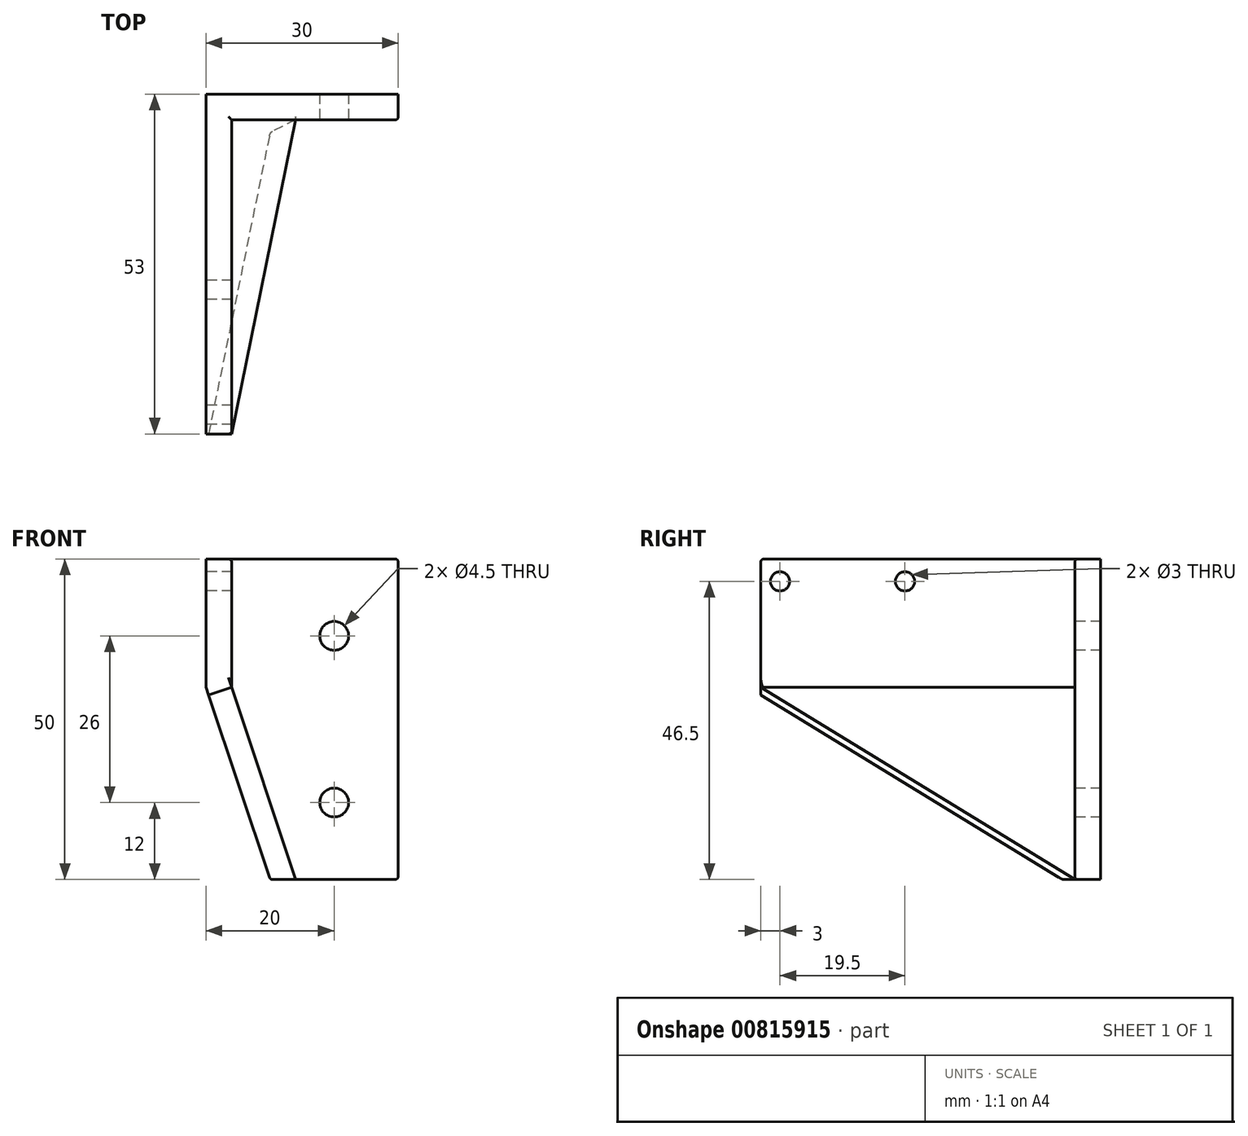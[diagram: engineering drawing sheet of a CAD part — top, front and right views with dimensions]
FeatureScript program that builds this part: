
annotation { "Feature Type Name" : "Feature", "Feature Type Description" : "" }
export const myFeature = defineFeature(function(context is Context, id is Id, definition is map)
    precondition{}
    {
        {
            var Q0;
            Q0=qCreatedBy(makeId("Front.planeOp"),FACE);
            var sketch = newSketch(context, id + "F0", { "sketchPlane" : qUnion([Q0])});
            skLineSegment(sketch, "E0.bottom", {"start": v(-15, 25) * mm, "end": v(15, 25) * mm});
            skLineSegment(sketch, "E0.top", {"start": v(-15, -25) * mm, "end": v(15, -25) * mm});
            skLineSegment(sketch, "E0.left", {"start": v(-15, 25) * mm, "end": v(-15, -25) * mm});
            skLineSegment(sketch, "E0.right", {"start": v(15, 25) * mm, "end": v(15, -25) * mm});
            skPoint(sketch, "E0.middle", {"position": v(0, 0) * mm});
            skLineSegment(sketch, "E1.bottom", {"start": v(-15, 25) * mm, "end": v(-11, 25) * mm});
            skLineSegment(sketch, "E1.top", {"start": v(-15, 5) * mm, "end": v(-11, 5) * mm});
            skLineSegment(sketch, "E1.left", {"start": v(-15, 25) * mm, "end": v(-15, 5) * mm});
            skLineSegment(sketch, "E1.right", {"start": v(-11, 25) * mm, "end": v(-11, 5) * mm});
            skCircle(sketch, "E2", {"center": v(5, 13) * mm, "radius": 2.25 * mm});
            skCircle(sketch, "E3", {"center": v(5, -13) * mm, "radius": 2.25 * mm});
            skPoint(sketch, "E4", {"position": v(-5, -25) * mm});
            skLineSegment(sketch, "E5", {"start": v(-15, 5) * mm, "end": v(-5, -25) * mm});
            skLineSegment(sketch, "E6", {"start": v(-11, 5) * mm, "end": v(-1, -25) * mm});
            skSolve(sketch);
        }
        {
            var Q0;
            {var subQ1=sQuery(id+"F0.wireOp",EDGE,"E0.right");Q0=makeQuery(id+"F0.imprint","IMPRINT",FACE,{"disambiguationData":[TD([[makeQuery(id+"F0.imprint","IMPRINT",EDGE,{"derivedFrom":subQ1}),-1.0]])]});}
            var Q1;
            {var subQ4=sQuery(id+"F0.wireOp",EDGE,"E1.top");Q1=makeQuery(id+"F0.imprint","IMPRINT",FACE,{"disambiguationData":[TD([[makeQuery(id+"F0.imprint","IMPRINT",EDGE,{"derivedFrom":subQ4}),1.0]])]});}
            var Q2;
            Q2=makeQuery(id+"F0.imprint","IMPRINT",FACE,{"disambiguationData":[TD([[makeQuery(id+"F0.imprint","IMPRINT",EDGE,{"derivedFrom":sQuery(id+"F0.wireOp",EDGE,"E1.top")}),-1.0]])]});
            extrude(context, id + "F1", {"entities" : qUnion([Q0, Q1, Q2]), "oppositeDirection" : true, "depth" : 4 * mm, "offsetDistance" : 25 * mm});
        }
        {
            var Q0;
            Q0=makeQuery(id+"F1.opExtrude","CAP_FACE",FACE,{"disambiguationData":[OSD([sQuery(id+"F0.wireOp",EDGE,"E0.bottom"),sQuery(id+"F0.wireOp",EDGE,"E0.top"),sQuery(id+"F0.wireOp",EDGE,"E0.left"),sQuery(id+"F0.wireOp",EDGE,"E0.right"),sQuery(id+"F0.wireOp",EDGE,"E2"),sQuery(id+"F0.wireOp",EDGE,"E3"),sQuery(id+"F0.wireOp",EDGE,"E5")])],"isStart":true});
            var sketch = newSketch(context, id + "F2", { "sketchPlane" : qUnion([Q0])});
            skLineSegment(sketch, "E7.bottom", {"start": v(-15, 25) * mm, "end": v(-11, 25) * mm});
            skLineSegment(sketch, "E7.top", {"start": v(-15, 5) * mm, "end": v(-11, 5) * mm});
            skLineSegment(sketch, "E7.left", {"start": v(-15, 25) * mm, "end": v(-15, 5) * mm});
            skLineSegment(sketch, "E7.right", {"start": v(-11, 25) * mm, "end": v(-11, 5) * mm});
            skLineSegment(sketch, "E8", {"start": v(-11, 5) * mm, "end": v(-1, -25) * mm});
            skSolve(sketch);
        }
        {
            var Q0;
            Q0 = qSketchRegion(id + "F2", true);
            var Q1;
            Q1=makeQuery(id+"F2.imprint","IMPRINT",FACE,{"disambiguationData":[TD([[makeQuery(id+"F2.imprint","IMPRINT",EDGE,{"derivedFrom":sQuery(id+"F2.wireOp",EDGE,"E7.top")}),-1.0]])]});
            extrude(context, id + "F3", {"entities" : qUnion([Q0, Q1]), "operationType" : NewBodyOperationType.ADD, "depth" : 49 * mm, "offsetDistance" : 25 * mm});
        }
        {
            var Q0;
            Q0=makeQuery(id+"F3.opExtrude","SWEPT_FACE",FACE,{"disambiguationData":[OSD([sQuery(id+"F2.wireOp",EDGE,"E8")])]});
            var sketch = newSketch(context, id + "F4", { "sketchPlane" : qUnion([Q0])});
            skLineSegment(sketch, "E9", {"start": v(-49, 8.22) * mm, "end": v(0, -23.4) * mm});
            skSolve(sketch);
        }
        {
            var Q0;
            Q0=makeQuery(id+"F4.imprint","IMPRINT",FACE,{"disambiguationData":[TD([[makeQuery(id+"F4.imprint","IMPRINT",EDGE,{"derivedFrom":sQuery(id+"F4.wireOp",EDGE,"E9")}),-1.0]])]});
            extrude(context, id + "F5", {"entities" : qUnion([Q0]), "operationType" : NewBodyOperationType.REMOVE, "endBound" : BoundingType.THROUGH_ALL, "oppositeDirection" : true, "depth" : 25 * mm, "offsetDistance" : 25 * mm});
        }
        {
            var Q0;
            Q0=makeQuery(id+"F3.opExtrude","CAP_EDGE",EDGE,{"disambiguationData":[OSD([sQuery(id+"F2.wireOp",EDGE,"E7.bottom")])],"isStart":false});
            var Q1;
            Q1=makeQuery(id+"F3.opExtrude","SWEPT_EDGE",EDGE,{"disambiguationData":[OSD([sQuery(id+"F0.wireOp",EDGE,"E0.bottom"),sQuery(id+"F2.wireOp",EDGE,"E7.bottom"),sQuery(id+"F2.wireOp",EDGE,"E7.right")])]});
            var Q2;
            Q2=makeQuery(id+"F1.opExtrude","CAP_EDGE",EDGE,{"disambiguationData":[OSD([sQuery(id+"F0.wireOp",EDGE,"E0.bottom")])],"isStart":true});
            var Q3;
            Q3=makeQuery(id+"F1.opExtrude","CAP_EDGE",EDGE,{"disambiguationData":[OSD([sQuery(id+"F0.wireOp",EDGE,"E0.right")])],"isStart":true});
            var Q4;
            Q4=makeQuery(id+"F1.opExtrude","SWEPT_EDGE",EDGE,{"disambiguationData":[OSD([sQuery(id+"F0.wireOp",EDGE,"E0.bottom"),sQuery(id+"F0.wireOp",EDGE,"E0.right")])]});
            var Q5;
            Q5=makeQuery(id+"F1.opExtrude","CAP_EDGE",EDGE,{"disambiguationData":[OSD([sQuery(id+"F0.wireOp",EDGE,"E0.top")])],"isStart":true});
            var Q6;
            Q6=makeQuery(id+"F3.opExtrude","CAP_EDGE",EDGE,{"disambiguationData":[OSD([sQuery(id+"F2.wireOp",EDGE,"E7.right")])],"isStart":false});
            var Q7;
            Q7=makeQuery(id+"F1.opExtrude","SWEPT_EDGE",EDGE,{"disambiguationData":[OSD([sQuery(id+"F0.wireOp",EDGE,"E0.top"),sQuery(id+"F0.wireOp",EDGE,"E0.right")])]});
            var Q8;
            {var subQ0=sQuery(id+"F0.wireOp",EDGE,"E5");var subQ1=sQuery(id+"F0.wireOp",EDGE,"E0.top");Q8=makeQuery(id+"F3.boolean.opBoolean","MERGE",EDGE,{"derivedFrom":[makeQuery(id+"F1.opExtrude","SWEPT_EDGE",EDGE,{"disambiguationData":[OSD([subQ1,subQ0])]}),makeQuery(id+"F3.opExtrude","SWEPT_EDGE",EDGE,{"disambiguationData":[OSD([subQ1,subQ0])]})]});}
            fillet(context, id + "F6", {"entities" : qUnion([Q0, Q1, Q2, Q3, Q4, Q5, Q6, Q7, Q8]), "radius" : .5 * mm, "tangentPropagation" : true, "allowEdgeOverflow" : false});
        }
        {
            var Q0;
            Q0=makeQuery(id+"F3.boolean.opBoolean","MERGE",FACE,{"derivedFrom":[makeQuery(id+"F1.opExtrude","SWEPT_FACE",FACE,{"disambiguationData":[OSD([sQuery(id+"F0.wireOp",EDGE,"E0.left")])]}),makeQuery(id+"F3.opExtrude","SWEPT_FACE",FACE,{"disambiguationData":[OSD([sQuery(id+"F2.wireOp",EDGE,"E7.left")])]})]});
            var sketch = newSketch(context, id + "F7", { "sketchPlane" : qUnion([Q0])});
            skCircle(sketch, "E10", {"center": v(46, 21.5) * mm, "radius": 1.5 * mm});
            skCircle(sketch, "E11", {"center": v(26.5, 21.5) * mm, "radius": 1.5 * mm});
            skSolve(sketch);
        }
        {
            var Q0;
            Q0=makeQuery(id+"F7.imprint","IMPRINT",FACE,{"disambiguationData":[TD([[makeQuery(id+"F7.imprint","IMPRINT",EDGE,{"derivedFrom":sQuery(id+"F7.wireOp",EDGE,"E11")}),1.0]])]});
            var Q1;
            Q1=makeQuery(id+"F7.imprint","IMPRINT",FACE,{"disambiguationData":[TD([[makeQuery(id+"F7.imprint","IMPRINT",EDGE,{"derivedFrom":sQuery(id+"F7.wireOp",EDGE,"E10")}),1.0]])]});
            extrude(context, id + "F8", {"entities" : qUnion([Q0, Q1]), "operationType" : NewBodyOperationType.REMOVE, "endBound" : BoundingType.THROUGH_ALL, "oppositeDirection" : true, "depth" : 25 * mm, "offsetDistance" : 25 * mm});
        }
    });
